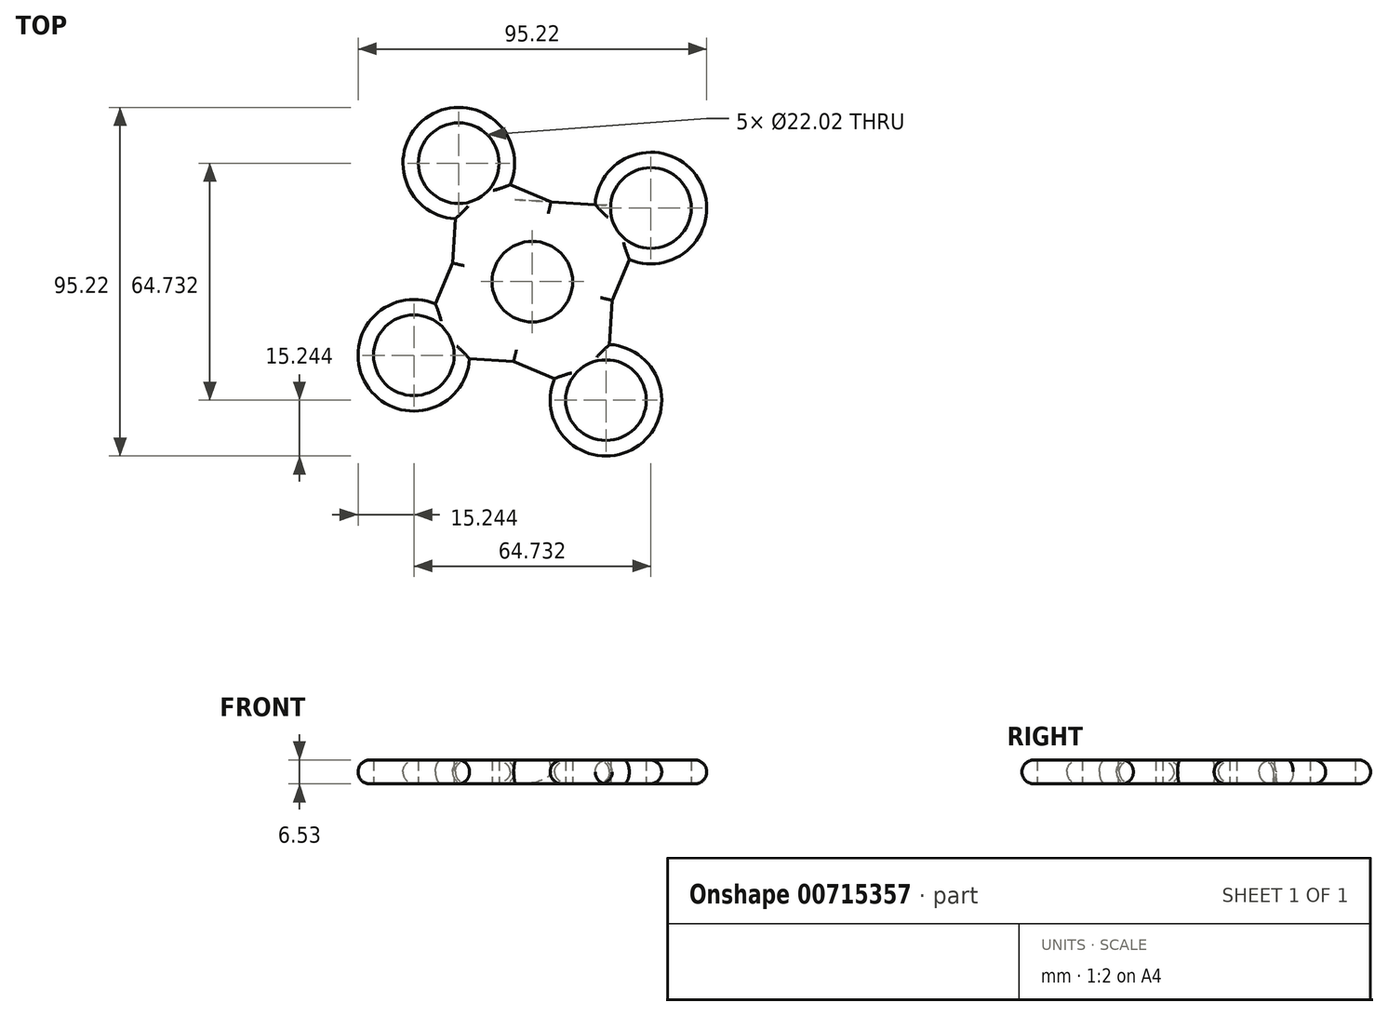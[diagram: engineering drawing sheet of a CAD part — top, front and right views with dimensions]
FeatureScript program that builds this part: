
annotation { "Feature Type Name" : "Feature", "Feature Type Description" : "" }
export const myFeature = defineFeature(function(context is Context, id is Id, definition is map)
    precondition{}
    {
        {
            var Q0;
            Q0=qCreatedBy(makeId("Top.planeOp"),FACE);
            var sketch = newSketch(context, id + "F0", { "sketchPlane" : qUnion([Q0])});
            skCircle(sketch, "E0", {"center": v(0, 0) * mm, "radius": 11.01 * mm});
            skCircle(sketch, "E1", {"center": v(-20.1, 32.37) * mm, "radius": 11.01 * mm});
            skCircle(sketch, "E2", {"center": v(32.37, 20.1) * mm, "radius": 11.01 * mm});
            skCircle(sketch, "E3", {"center": v(20.1, -32.37) * mm, "radius": 11.01 * mm});
            skCircle(sketch, "E4", {"center": v(-32.37, -20.1) * mm, "radius": 11.01 * mm});
            skLineSegment(sketch, "E5", {"start": v(21.05, -17.16) * mm, "end": v(21.8, -5.1) * mm});
            skLineSegment(sketch, "E6", {"start": v(6.05, -26.47) * mm, "end": v(-5.1, -21.8) * mm});
            skLineSegment(sketch, "E7", {"start": v(-17.16, -21.05) * mm, "end": v(-5.1, -21.8) * mm});
            skLineSegment(sketch, "E8", {"start": v(-26.47, -6.05) * mm, "end": v(-21.8, 5.1) * mm});
            skLineSegment(sketch, "E9", {"start": v(-21.05, 17.16) * mm, "end": v(-21.8, 5.1) * mm});
            skLineSegment(sketch, "E10", {"start": v(-6.05, 26.47) * mm, "end": v(5.1, 21.8) * mm});
            skLineSegment(sketch, "E11", {"start": v(17.16, 21.05) * mm, "end": v(5.1, 21.8) * mm});
            skLineSegment(sketch, "E12", {"start": v(26.47, 6.05) * mm, "end": v(21.8, -5.1) * mm});
            skArc(sketch, "E13", {"start": v(-6.05, 26.47) * mm, "mid": v(-28.14, 45.31) * mm, "end": v(-21.05, 17.16) * mm});
            skArc(sketch, "E14", {"start": v(26.47, 6.05) * mm, "mid": v(45.31, 28.14) * mm, "end": v(17.16, 21.05) * mm});
            skArc(sketch, "E15", {"start": v(6.05, -26.47) * mm, "mid": v(28.14, -45.31) * mm, "end": v(21.05, -17.16) * mm});
            skArc(sketch, "E16", {"start": v(-26.47, -6.05) * mm, "mid": v(-45.31, -28.14) * mm, "end": v(-17.16, -21.05) * mm});
            skSolve(sketch);
        }
        {
            var Q0;
            {var subQ0=sQuery(id+"F0.wireOp",EDGE,"E9");var subQ1=sQuery(id+"F0.wireOp",EDGE,"E1");var subQ2=makeQuery(id+"F0.imprint","INTERSECT",VERTEX,{"derivedFrom":[subQ1,subQ0]});Q0=makeQuery(id+"F0.imprint","IMPRINT",FACE,{"disambiguationData":[TD([[makeQuery(id+"F0.imprint","IMPRINT",EDGE,{"disambiguationData":[TD([[subQ2,1.0]])],"derivedFrom":subQ1}),-1.0]])]});}
            var Q1;
            {var subQ3=sQuery(id+"F0.wireOp",EDGE,"E10");var subQ5=sQuery(id+"F0.wireOp",EDGE,"E13");var subQ7=makeQuery(id+"F0.imprint","INTERSECT",VERTEX,{"derivedFrom":[subQ3,subQ5]});Q1=makeQuery(id+"F0.imprint","IMPRINT",FACE,{"disambiguationData":[TD([[makeQuery(id+"F0.imprint","IMPRINT",EDGE,{"disambiguationData":[TD([[subQ7,1.0]])],"derivedFrom":subQ3}),-1.0]])]});}
            var Q2;
            {var subQ3=sQuery(id+"F0.wireOp",EDGE,"E9");var subQ5=sQuery(id+"F0.wireOp",EDGE,"E13");var subQ7=makeQuery(id+"F0.imprint","INTERSECT",VERTEX,{"derivedFrom":[subQ3,subQ5]});Q2=makeQuery(id+"F0.imprint","IMPRINT",FACE,{"disambiguationData":[TD([[makeQuery(id+"F0.imprint","IMPRINT",EDGE,{"disambiguationData":[TD([[subQ7,1.0]])],"derivedFrom":subQ3}),1.0]])]});}
            var Q3;
            {var subQ1=sQuery(id+"F0.wireOp",EDGE,"5QycCs7I-3Amh-WNx4-8zut-PG4qwJrJAVW8");var subQ3=sQuery(id+"F0.wireOp",EDGE,"E13");var subQ4=makeQuery(id+"F0.imprint","INTERSECT",VERTEX,{"derivedFrom":[subQ1,subQ3]});Q3=makeQuery(id+"F0.imprint","IMPRINT",FACE,{"disambiguationData":[TD([[makeQuery(id+"F0.imprint","IMPRINT",EDGE,{"disambiguationData":[TD([[subQ4,1.0]])],"derivedFrom":subQ3}),1.0]])]});}
            var Q4;
            {var subQ1=sQuery(id+"F0.wireOp",EDGE,"5QycCs7I-3Amh-WNx4-8zut-PG4qwJrJAVW8");var subQ3=sQuery(id+"F0.wireOp",EDGE,"E13");var subQ4=makeQuery(id+"F0.imprint","INTERSECT",VERTEX,{"derivedFrom":[subQ1,subQ3]});Q4=makeQuery(id+"F0.imprint","IMPRINT",FACE,{"disambiguationData":[TD([[makeQuery(id+"F0.imprint","IMPRINT",EDGE,{"disambiguationData":[TD([[subQ4,-1.0]])],"derivedFrom":subQ3}),1.0]])]});}
            var Q5;
            {var subQ5=sQuery(id+"F0.wireOp",EDGE,"E0");var subQ6=sQuery(id+"F0.wireOp",EDGE,"YydM656u-WZQG-gHOT-9s7W-Rua28V6mmtaj");var subQ7=makeQuery(id+"F0.imprint","INTERSECT",VERTEX,{"derivedFrom":[subQ6,subQ5]});Q5=makeQuery(id+"F0.imprint","IMPRINT",FACE,{"disambiguationData":[TD([[makeQuery(id+"F0.imprint","IMPRINT",EDGE,{"disambiguationData":[TD([[subQ7,-1.0]])],"derivedFrom":subQ6}),1.0]])]});}
            var Q6;
            {var subQ5=sQuery(id+"F0.wireOp",EDGE,"E0");var subQ6=sQuery(id+"F0.wireOp",EDGE,"te8bgYfq-3EHM-nhbH-NchS-k7L6vqbxxhMY");var subQ7=makeQuery(id+"F0.imprint","INTERSECT",VERTEX,{"derivedFrom":[subQ6,subQ5]});Q6=makeQuery(id+"F0.imprint","IMPRINT",FACE,{"disambiguationData":[TD([[makeQuery(id+"F0.imprint","IMPRINT",EDGE,{"disambiguationData":[TD([[subQ7,-1.0]])],"derivedFrom":subQ6}),-1.0]])]});}
            var Q7;
            {var subQ0=sQuery(id+"F0.wireOp",EDGE,"E9");var subQ1=sQuery(id+"F0.wireOp",EDGE,"E8");var subQ2=makeQuery(id+"F0.imprint","INTERSECT",VERTEX,{"derivedFrom":[subQ1,subQ0]});Q7=makeQuery(id+"F0.imprint","IMPRINT",FACE,{"disambiguationData":[TD([[makeQuery(id+"F0.imprint","IMPRINT",EDGE,{"disambiguationData":[TD([[subQ2,-1.0]])],"derivedFrom":subQ1}),1.0]])]});}
            var Q8;
            {var subQ0=sQuery(id+"F0.wireOp",EDGE,"E13");var subQ1=sQuery(id+"F0.wireOp",EDGE,"E10");var subQ2=makeQuery(id+"F0.imprint","INTERSECT",VERTEX,{"derivedFrom":[subQ1,subQ0]});Q8=makeQuery(id+"F0.imprint","IMPRINT",FACE,{"disambiguationData":[TD([[makeQuery(id+"F0.imprint","IMPRINT",EDGE,{"disambiguationData":[TD([[subQ2,-1.0]])],"derivedFrom":subQ1}),-1.0]])]});}
            var Q9;
            {var subQ0=sQuery(id+"F0.wireOp",EDGE,"E11");var subQ1=sQuery(id+"F0.wireOp",EDGE,"E10");var subQ2=makeQuery(id+"F0.imprint","INTERSECT",VERTEX,{"derivedFrom":[subQ1,subQ0]});Q9=makeQuery(id+"F0.imprint","IMPRINT",FACE,{"disambiguationData":[TD([[makeQuery(id+"F0.imprint","IMPRINT",EDGE,{"disambiguationData":[TD([[subQ2,-1.0]])],"derivedFrom":subQ1}),1.0]])]});}
            var Q10;
            {var subQ3=sQuery(id+"F0.wireOp",EDGE,"E11");var subQ5=sQuery(id+"F0.wireOp",EDGE,"E14");var subQ6=makeQuery(id+"F0.imprint","INTERSECT",VERTEX,{"derivedFrom":[subQ3,subQ5]});Q10=makeQuery(id+"F0.imprint","IMPRINT",FACE,{"disambiguationData":[TD([[makeQuery(id+"F0.imprint","IMPRINT",EDGE,{"disambiguationData":[TD([[subQ6,1.0]])],"derivedFrom":subQ3}),1.0]])]});}
            var Q11;
            {var subQ0=sQuery(id+"F0.wireOp",EDGE,"E11");var subQ1=sQuery(id+"F0.wireOp",EDGE,"E2");var subQ2=makeQuery(id+"F0.imprint","INTERSECT",VERTEX,{"derivedFrom":[subQ1,subQ0]});Q11=makeQuery(id+"F0.imprint","IMPRINT",FACE,{"disambiguationData":[TD([[makeQuery(id+"F0.imprint","IMPRINT",EDGE,{"disambiguationData":[TD([[subQ2,1.0]])],"derivedFrom":subQ1}),-1.0]])]});}
            var Q12;
            {var subQ3=sQuery(id+"F0.wireOp",EDGE,"E12");var subQ5=sQuery(id+"F0.wireOp",EDGE,"E14");var subQ7=makeQuery(id+"F0.imprint","INTERSECT",VERTEX,{"derivedFrom":[subQ3,subQ5]});Q12=makeQuery(id+"F0.imprint","IMPRINT",FACE,{"disambiguationData":[TD([[makeQuery(id+"F0.imprint","IMPRINT",EDGE,{"disambiguationData":[TD([[subQ7,1.0]])],"derivedFrom":subQ3}),-1.0]])]});}
            var Q13;
            {var subQ0=sQuery(id+"F0.wireOp",EDGE,"E0");var subQ1=sQuery(id+"F0.wireOp",EDGE,"Z5p2u8Yq-H2cL-9i6f-NE9L-ZFUaDijVdvWC");var subQ2=makeQuery(id+"F0.imprint","INTERSECT",VERTEX,{"derivedFrom":[subQ1,subQ0]});Q13=makeQuery(id+"F0.imprint","IMPRINT",FACE,{"disambiguationData":[TD([[makeQuery(id+"F0.imprint","IMPRINT",EDGE,{"disambiguationData":[TD([[subQ2,-1.0]])],"derivedFrom":subQ1}),1.0]])]});}
            var Q14;
            {var subQ1=sQuery(id+"F0.wireOp",EDGE,"YydM656u-WZQG-gHOT-9s7W-Rua28V6mmtaj");var subQ3=sQuery(id+"F0.wireOp",EDGE,"E14");var subQ4=makeQuery(id+"F0.imprint","INTERSECT",VERTEX,{"derivedFrom":[subQ1,subQ3]});Q14=makeQuery(id+"F0.imprint","IMPRINT",FACE,{"disambiguationData":[TD([[makeQuery(id+"F0.imprint","IMPRINT",EDGE,{"disambiguationData":[TD([[subQ4,-1.0]])],"derivedFrom":subQ3}),1.0]])]});}
            var Q15;
            {var subQ0=sQuery(id+"F0.wireOp",EDGE,"E12");var subQ1=sQuery(id+"F0.wireOp",EDGE,"E5");var subQ2=makeQuery(id+"F0.imprint","INTERSECT",VERTEX,{"derivedFrom":[subQ1,subQ0]});Q15=makeQuery(id+"F0.imprint","IMPRINT",FACE,{"disambiguationData":[TD([[makeQuery(id+"F0.imprint","IMPRINT",EDGE,{"disambiguationData":[TD([[subQ2,-1.0]])],"derivedFrom":subQ1}),-1.0]])]});}
            var Q16;
            {var subQ1=sQuery(id+"F0.wireOp",EDGE,"YydM656u-WZQG-gHOT-9s7W-Rua28V6mmtaj");var subQ3=sQuery(id+"F0.wireOp",EDGE,"E14");var subQ4=makeQuery(id+"F0.imprint","INTERSECT",VERTEX,{"derivedFrom":[subQ1,subQ3]});Q16=makeQuery(id+"F0.imprint","IMPRINT",FACE,{"disambiguationData":[TD([[makeQuery(id+"F0.imprint","IMPRINT",EDGE,{"disambiguationData":[TD([[subQ4,1.0]])],"derivedFrom":subQ3}),1.0]])]});}
            var Q17;
            {var subQ0=sQuery(id+"F0.wireOp",EDGE,"E15");var subQ1=sQuery(id+"F0.wireOp",EDGE,"E5");var subQ2=makeQuery(id+"F0.imprint","INTERSECT",VERTEX,{"derivedFrom":[subQ1,subQ0]});Q17=makeQuery(id+"F0.imprint","IMPRINT",FACE,{"disambiguationData":[TD([[makeQuery(id+"F0.imprint","IMPRINT",EDGE,{"disambiguationData":[TD([[subQ2,-1.0]])],"derivedFrom":subQ1}),1.0]])]});}
            var Q18;
            {var subQ3=sQuery(id+"F0.wireOp",EDGE,"E5");var subQ5=sQuery(id+"F0.wireOp",EDGE,"E15");var subQ7=makeQuery(id+"F0.imprint","INTERSECT",VERTEX,{"derivedFrom":[subQ3,subQ5]});Q18=makeQuery(id+"F0.imprint","IMPRINT",FACE,{"disambiguationData":[TD([[makeQuery(id+"F0.imprint","IMPRINT",EDGE,{"disambiguationData":[TD([[subQ7,1.0]])],"derivedFrom":subQ3}),1.0]])]});}
            var Q19;
            {var subQ0=sQuery(id+"F0.wireOp",EDGE,"E5");var subQ1=sQuery(id+"F0.wireOp",EDGE,"E3");var subQ2=makeQuery(id+"F0.imprint","INTERSECT",VERTEX,{"derivedFrom":[subQ1,subQ0]});Q19=makeQuery(id+"F0.imprint","IMPRINT",FACE,{"disambiguationData":[TD([[makeQuery(id+"F0.imprint","IMPRINT",EDGE,{"disambiguationData":[TD([[subQ2,1.0]])],"derivedFrom":subQ1}),-1.0]])]});}
            var Q20;
            {var subQ1=sQuery(id+"F0.wireOp",EDGE,"Z5p2u8Yq-H2cL-9i6f-NE9L-ZFUaDijVdvWC");var subQ3=sQuery(id+"F0.wireOp",EDGE,"E15");var subQ4=makeQuery(id+"F0.imprint","INTERSECT",VERTEX,{"derivedFrom":[subQ1,subQ3]});Q20=makeQuery(id+"F0.imprint","IMPRINT",FACE,{"disambiguationData":[TD([[makeQuery(id+"F0.imprint","IMPRINT",EDGE,{"disambiguationData":[TD([[subQ4,1.0]])],"derivedFrom":subQ3}),1.0]])]});}
            var Q21;
            {var subQ3=sQuery(id+"F0.wireOp",EDGE,"E6");var subQ5=sQuery(id+"F0.wireOp",EDGE,"E15");var subQ6=makeQuery(id+"F0.imprint","INTERSECT",VERTEX,{"derivedFrom":[subQ3,subQ5]});Q21=makeQuery(id+"F0.imprint","IMPRINT",FACE,{"disambiguationData":[TD([[makeQuery(id+"F0.imprint","IMPRINT",EDGE,{"disambiguationData":[TD([[subQ6,1.0]])],"derivedFrom":subQ3}),-1.0]])]});}
            var Q22;
            {var subQ1=sQuery(id+"F0.wireOp",EDGE,"Z5p2u8Yq-H2cL-9i6f-NE9L-ZFUaDijVdvWC");var subQ3=sQuery(id+"F0.wireOp",EDGE,"E15");var subQ4=makeQuery(id+"F0.imprint","INTERSECT",VERTEX,{"derivedFrom":[subQ1,subQ3]});Q22=makeQuery(id+"F0.imprint","IMPRINT",FACE,{"disambiguationData":[TD([[makeQuery(id+"F0.imprint","IMPRINT",EDGE,{"disambiguationData":[TD([[subQ4,-1.0]])],"derivedFrom":subQ3}),1.0]])]});}
            var Q23;
            {var subQ0=sQuery(id+"F0.wireOp",EDGE,"E0");var subQ1=sQuery(id+"F0.wireOp",EDGE,"te8bgYfq-3EHM-nhbH-NchS-k7L6vqbxxhMY");var subQ2=makeQuery(id+"F0.imprint","INTERSECT",VERTEX,{"derivedFrom":[subQ1,subQ0]});Q23=makeQuery(id+"F0.imprint","IMPRINT",FACE,{"disambiguationData":[TD([[makeQuery(id+"F0.imprint","IMPRINT",EDGE,{"disambiguationData":[TD([[subQ2,-1.0]])],"derivedFrom":subQ1}),1.0]])]});}
            var Q24;
            {var subQ3=sQuery(id+"F0.wireOp",EDGE,"E7");var subQ5=sQuery(id+"F0.wireOp",EDGE,"E16");var subQ7=makeQuery(id+"F0.imprint","INTERSECT",VERTEX,{"derivedFrom":[subQ3,subQ5]});Q24=makeQuery(id+"F0.imprint","IMPRINT",FACE,{"disambiguationData":[TD([[makeQuery(id+"F0.imprint","IMPRINT",EDGE,{"disambiguationData":[TD([[subQ7,1.0]])],"derivedFrom":subQ3}),1.0]])]});}
            var Q25;
            {var subQ1=sQuery(id+"F0.wireOp",EDGE,"te8bgYfq-3EHM-nhbH-NchS-k7L6vqbxxhMY");var subQ3=sQuery(id+"F0.wireOp",EDGE,"E16");var subQ4=makeQuery(id+"F0.imprint","INTERSECT",VERTEX,{"derivedFrom":[subQ1,subQ3]});Q25=makeQuery(id+"F0.imprint","IMPRINT",FACE,{"disambiguationData":[TD([[makeQuery(id+"F0.imprint","IMPRINT",EDGE,{"disambiguationData":[TD([[subQ4,1.0]])],"derivedFrom":subQ3}),1.0]])]});}
            var Q26;
            {var subQ3=sQuery(id+"F0.wireOp",EDGE,"E8");var subQ5=sQuery(id+"F0.wireOp",EDGE,"E16");var subQ6=makeQuery(id+"F0.imprint","INTERSECT",VERTEX,{"derivedFrom":[subQ3,subQ5]});Q26=makeQuery(id+"F0.imprint","IMPRINT",FACE,{"disambiguationData":[TD([[makeQuery(id+"F0.imprint","IMPRINT",EDGE,{"disambiguationData":[TD([[subQ6,1.0]])],"derivedFrom":subQ3}),-1.0]])]});}
            var Q27;
            {var subQ1=sQuery(id+"F0.wireOp",EDGE,"te8bgYfq-3EHM-nhbH-NchS-k7L6vqbxxhMY");var subQ3=sQuery(id+"F0.wireOp",EDGE,"E16");var subQ4=makeQuery(id+"F0.imprint","INTERSECT",VERTEX,{"derivedFrom":[subQ1,subQ3]});Q27=makeQuery(id+"F0.imprint","IMPRINT",FACE,{"disambiguationData":[TD([[makeQuery(id+"F0.imprint","IMPRINT",EDGE,{"disambiguationData":[TD([[subQ4,-1.0]])],"derivedFrom":subQ3}),1.0]])]});}
            var Q28;
            {var subQ0=sQuery(id+"F0.wireOp",EDGE,"E8");var subQ1=sQuery(id+"F0.wireOp",EDGE,"E4");var subQ2=makeQuery(id+"F0.imprint","INTERSECT",VERTEX,{"derivedFrom":[subQ1,subQ0]});Q28=makeQuery(id+"F0.imprint","IMPRINT",FACE,{"disambiguationData":[TD([[makeQuery(id+"F0.imprint","IMPRINT",EDGE,{"disambiguationData":[TD([[subQ2,-1.0]])],"derivedFrom":subQ1}),-1.0]])]});}
            var Q29;
            {var subQ0=sQuery(id+"F0.wireOp",EDGE,"E7");var subQ1=sQuery(id+"F0.wireOp",EDGE,"E6");var subQ2=makeQuery(id+"F0.imprint","INTERSECT",VERTEX,{"derivedFrom":[subQ1,subQ0]});Q29=makeQuery(id+"F0.imprint","IMPRINT",FACE,{"disambiguationData":[TD([[makeQuery(id+"F0.imprint","IMPRINT",EDGE,{"disambiguationData":[TD([[subQ2,-1.0]])],"derivedFrom":subQ1}),1.0]])]});}
            var Q30;
            {var subQ0=sQuery(id+"F0.wireOp",EDGE,"E16");var subQ1=sQuery(id+"F0.wireOp",EDGE,"E8");var subQ2=makeQuery(id+"F0.imprint","INTERSECT",VERTEX,{"derivedFrom":[subQ1,subQ0]});Q30=makeQuery(id+"F0.imprint","IMPRINT",FACE,{"disambiguationData":[TD([[makeQuery(id+"F0.imprint","IMPRINT",EDGE,{"disambiguationData":[TD([[subQ2,-1.0]])],"derivedFrom":subQ1}),-1.0]])]});}
            var Q31;
            {var subQ0=sQuery(id+"F0.wireOp",EDGE,"E15");var subQ1=sQuery(id+"F0.wireOp",EDGE,"E6");var subQ2=makeQuery(id+"F0.imprint","INTERSECT",VERTEX,{"derivedFrom":[subQ1,subQ0]});Q31=makeQuery(id+"F0.imprint","IMPRINT",FACE,{"disambiguationData":[TD([[makeQuery(id+"F0.imprint","IMPRINT",EDGE,{"disambiguationData":[TD([[subQ2,-1.0]])],"derivedFrom":subQ1}),-1.0]])]});}
            extrude(context, id + "F1", {"entities" : qUnion([Q0, Q1, Q2, Q3, Q4, Q5, Q6, Q7, Q8, Q9, Q10, Q11, Q12, Q13, Q14, Q15, Q16, Q17, Q18, Q19, Q20, Q21, Q22, Q23, Q24, Q25, Q26, Q27, Q28, Q29, Q30, Q31]), "depth" : 6.53 * mm, "offsetDistance" : 25.4 * mm});
        }
        {
            var Q0;
            Q0=makeQuery(id+"F1.opExtrude","CAP_EDGE",EDGE,{"disambiguationData":[OSD([sQuery(id+"F0.wireOp",EDGE,"E9")])],"isStart":false});
            var Q1;
            Q1=makeQuery(id+"F1.opExtrude","CAP_EDGE",EDGE,{"disambiguationData":[OSD([sQuery(id+"F0.wireOp",EDGE,"E8")])],"isStart":false});
            var Q2;
            Q2=makeQuery(id+"F1.opExtrude","CAP_EDGE",EDGE,{"disambiguationData":[OSD([sQuery(id+"F0.wireOp",EDGE,"E13")])],"isStart":false});
            var Q3;
            Q3=makeQuery(id+"F1.opExtrude","CAP_EDGE",EDGE,{"disambiguationData":[OSD([sQuery(id+"F0.wireOp",EDGE,"E10")])],"isStart":false});
            var Q4;
            Q4=makeQuery(id+"F1.opExtrude","CAP_EDGE",EDGE,{"disambiguationData":[OSD([sQuery(id+"F0.wireOp",EDGE,"E11")])],"isStart":false});
            var Q5;
            Q5=makeQuery(id+"F1.opExtrude","CAP_EDGE",EDGE,{"disambiguationData":[OSD([sQuery(id+"F0.wireOp",EDGE,"E14")])],"isStart":false});
            var Q6;
            Q6=makeQuery(id+"F1.opExtrude","CAP_EDGE",EDGE,{"disambiguationData":[OSD([sQuery(id+"F0.wireOp",EDGE,"E12")])],"isStart":false});
            var Q7;
            Q7=makeQuery(id+"F1.opExtrude","CAP_EDGE",EDGE,{"disambiguationData":[OSD([sQuery(id+"F0.wireOp",EDGE,"E5")])],"isStart":false});
            var Q8;
            Q8=makeQuery(id+"F1.opExtrude","CAP_EDGE",EDGE,{"disambiguationData":[OSD([sQuery(id+"F0.wireOp",EDGE,"E15")])],"isStart":false});
            var Q9;
            Q9=makeQuery(id+"F1.opExtrude","CAP_EDGE",EDGE,{"disambiguationData":[OSD([sQuery(id+"F0.wireOp",EDGE,"E6")])],"isStart":false});
            var Q10;
            Q10=makeQuery(id+"F1.opExtrude","CAP_EDGE",EDGE,{"disambiguationData":[OSD([sQuery(id+"F0.wireOp",EDGE,"E7")])],"isStart":false});
            var Q11;
            Q11=makeQuery(id+"F1.opExtrude","CAP_EDGE",EDGE,{"disambiguationData":[OSD([sQuery(id+"F0.wireOp",EDGE,"E16")])],"isStart":false});
            var Q12;
            Q12=makeQuery(id+"F1.opExtrude","CAP_EDGE",EDGE,{"disambiguationData":[OSD([sQuery(id+"F0.wireOp",EDGE,"E13")])],"isStart":true});
            var Q13;
            Q13=makeQuery(id+"F1.opExtrude","CAP_EDGE",EDGE,{"disambiguationData":[OSD([sQuery(id+"F0.wireOp",EDGE,"E10")])],"isStart":true});
            var Q14;
            Q14=makeQuery(id+"F1.opExtrude","CAP_EDGE",EDGE,{"disambiguationData":[OSD([sQuery(id+"F0.wireOp",EDGE,"E14")])],"isStart":true});
            var Q15;
            Q15=makeQuery(id+"F1.opExtrude","CAP_EDGE",EDGE,{"disambiguationData":[OSD([sQuery(id+"F0.wireOp",EDGE,"E12")])],"isStart":true});
            var Q16;
            Q16=makeQuery(id+"F1.opExtrude","CAP_EDGE",EDGE,{"disambiguationData":[OSD([sQuery(id+"F0.wireOp",EDGE,"E5")])],"isStart":true});
            var Q17;
            Q17=makeQuery(id+"F1.opExtrude","CAP_EDGE",EDGE,{"disambiguationData":[OSD([sQuery(id+"F0.wireOp",EDGE,"E15")])],"isStart":true});
            var Q18;
            Q18=makeQuery(id+"F1.opExtrude","CAP_EDGE",EDGE,{"disambiguationData":[OSD([sQuery(id+"F0.wireOp",EDGE,"E6")])],"isStart":true});
            var Q19;
            Q19=makeQuery(id+"F1.opExtrude","CAP_EDGE",EDGE,{"disambiguationData":[OSD([sQuery(id+"F0.wireOp",EDGE,"E7")])],"isStart":true});
            var Q20;
            Q20=makeQuery(id+"F1.opExtrude","CAP_EDGE",EDGE,{"disambiguationData":[OSD([sQuery(id+"F0.wireOp",EDGE,"E16")])],"isStart":true});
            var Q21;
            Q21=makeQuery(id+"F1.opExtrude","CAP_EDGE",EDGE,{"disambiguationData":[OSD([sQuery(id+"F0.wireOp",EDGE,"E8")])],"isStart":true});
            var Q22;
            Q22=makeQuery(id+"F1.opExtrude","CAP_EDGE",EDGE,{"disambiguationData":[OSD([sQuery(id+"F0.wireOp",EDGE,"E9")])],"isStart":true});
            fillet(context, id + "F2", {"entities" : qUnion([Q0, Q1, Q2, Q3, Q4, Q5, Q6, Q7, Q8, Q9, Q10, Q11, Q12, Q13, Q14, Q15, Q16, Q17, Q18, Q19, Q20, Q21, Q22]), "radius" : 3.25 * mm, "tangentPropagation" : true, "allowEdgeOverflow" : false});
        }
    });
